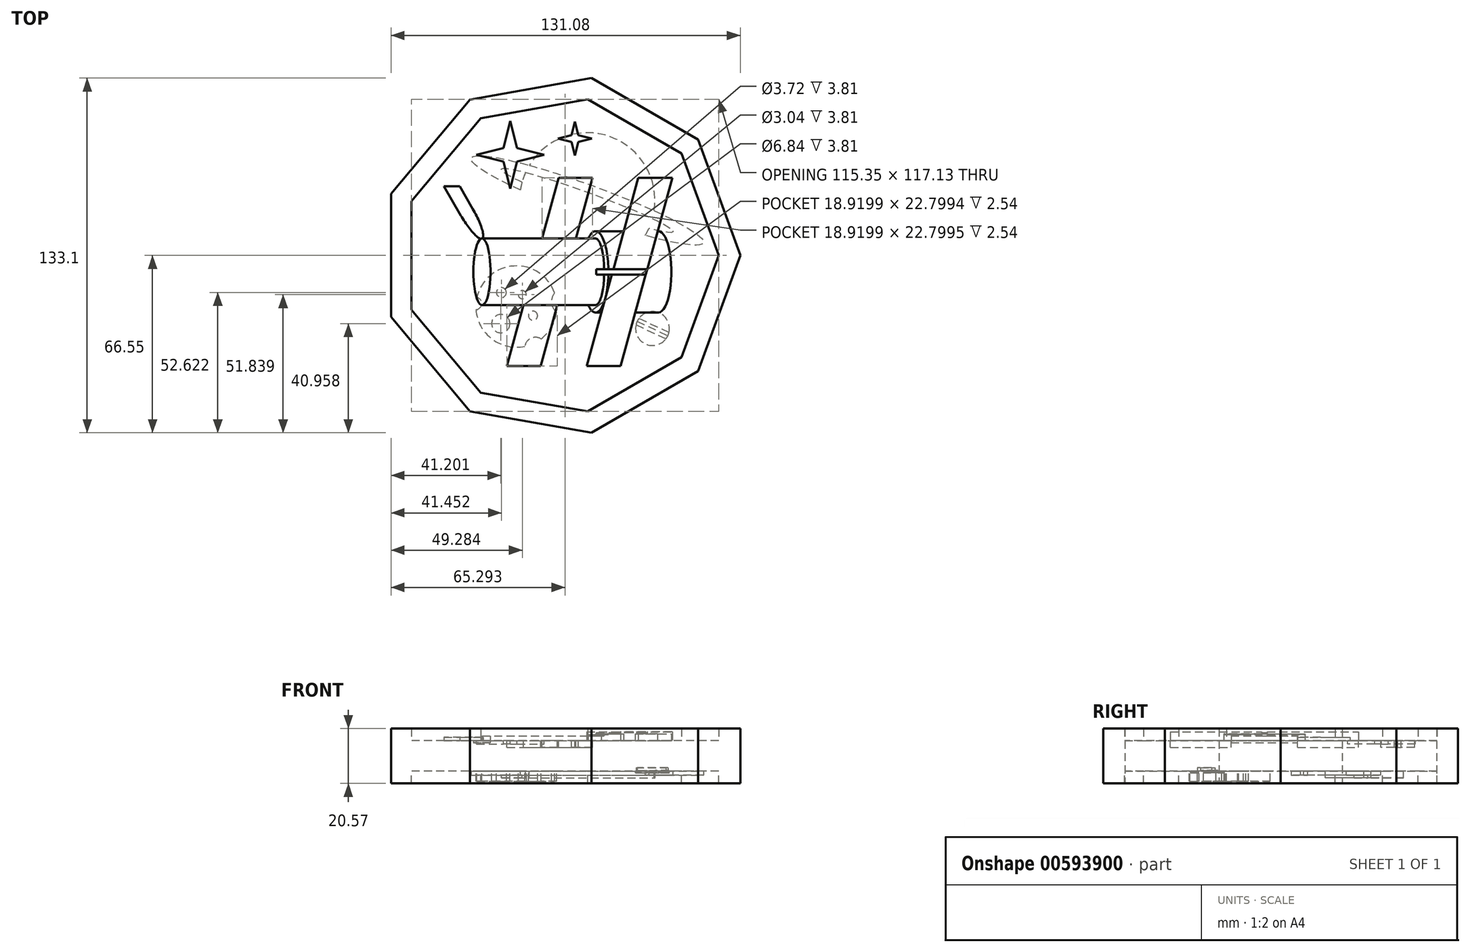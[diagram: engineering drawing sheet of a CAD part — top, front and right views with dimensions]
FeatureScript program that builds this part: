
annotation { "Feature Type Name" : "Feature", "Feature Type Description" : "" }
export const myFeature = defineFeature(function(context is Context, id is Id, definition is map)
    precondition{}
    {
        {
            var Q0;
            Q0=qCreatedBy(makeId("Top.planeOp"),FACE);
            var sketch = newSketch(context, id + "F0", { "sketchPlane" : qUnion([Q0])});
            skCircle(sketch, "E0.cCircle", {"center": v(0, 0) * mm, "radius": 63.5 * mm, "construction": true});
            skLineSegment(sketch, "E0.0", {"start": v(-63.5, -23.11) * mm, "end": v(-63.5, 23.11) * mm});
            skLineSegment(sketch, "E0.1", {"start": v(-63.5, 23.11) * mm, "end": v(-33.79, 58.52) * mm});
            skLineSegment(sketch, "E0.2", {"start": v(-33.79, 58.52) * mm, "end": v(11.73, 66.55) * mm});
            skLineSegment(sketch, "E0.3", {"start": v(11.73, 66.55) * mm, "end": v(51.77, 43.44) * mm});
            skLineSegment(sketch, "E0.4", {"start": v(51.77, 43.44) * mm, "end": v(67.58, 0) * mm});
            skLineSegment(sketch, "E0.5", {"start": v(67.58, 0) * mm, "end": v(51.77, -43.44) * mm});
            skLineSegment(sketch, "E0.6", {"start": v(51.77, -43.44) * mm, "end": v(11.73, -66.55) * mm});
            skLineSegment(sketch, "E0.7", {"start": v(11.73, -66.55) * mm, "end": v(-33.79, -58.52) * mm});
            skLineSegment(sketch, "E0.8", {"start": v(-33.79, -58.52) * mm, "end": v(-63.5, -23.11) * mm});
            skPoint(sketch, "E0.0.midPoint", {"position": v(-63.5, 0) * mm});
            skSolve(sketch);
        }
        {
            var Q0;
            Q0=makeQuery(id+"F0.imprint","IMPRINT",FACE,{"disambiguationData":[TD([[makeQuery(id+"F0.imprint","IMPRINT",EDGE,{"derivedFrom":sQuery(id+"F0.wireOp",EDGE,"E0.0")}),-1.0]])]});
            var sketch = newSketch(context, id + "F1", { "sketchPlane" : qUnion([Q0])});
            skCircle(sketch, "E1.cCircle", {"center": v(0, 0) * mm, "radius": 57.8 * mm, "construction": true});
            skLineSegment(sketch, "E1.0", {"start": v(-57.8, -21.04) * mm, "end": v(-57.8, 21.04) * mm});
            skLineSegment(sketch, "E1.1", {"start": v(-57.8, 21.04) * mm, "end": v(-30.76, 53.27) * mm});
            skLineSegment(sketch, "E1.2", {"start": v(-30.76, 53.27) * mm, "end": v(10.68, 60.58) * mm});
            skLineSegment(sketch, "E1.3", {"start": v(10.68, 60.58) * mm, "end": v(47.12, 39.54) * mm});
            skLineSegment(sketch, "E1.4", {"start": v(47.12, 39.54) * mm, "end": v(61.52, 0) * mm});
            skLineSegment(sketch, "E1.5", {"start": v(61.52, 0) * mm, "end": v(47.12, -39.54) * mm});
            skLineSegment(sketch, "E1.6", {"start": v(47.12, -39.54) * mm, "end": v(10.68, -60.58) * mm});
            skLineSegment(sketch, "E1.7", {"start": v(10.68, -60.58) * mm, "end": v(-30.76, -53.27) * mm});
            skLineSegment(sketch, "E1.8", {"start": v(-30.76, -53.27) * mm, "end": v(-57.8, -21.04) * mm});
            skPoint(sketch, "E1.0.midPoint", {"position": v(-57.8, 0) * mm});
            skSolve(sketch);
        }
        {
            var Q0;
            Q0=makeQuery(id+"F1.imprint","IMPRINT",FACE,{"disambiguationData":[TD([[makeQuery(id+"F1.imprint","IMPRINT",EDGE,{"derivedFrom":sQuery(id+"F1.wireOp",EDGE,"E1.0")}),1.0]])]});
            var Q1;
            Q1=makeQuery(id+"F1.imprint","IMPRINT",FACE,{"disambiguationData":[TD([[makeQuery(id+"F1.imprint","IMPRINT",EDGE,{"derivedFrom":sQuery(id+"F1.wireOp",EDGE,"E1.0")}),-1.0]])]});
            extrude(context, id + "F2", {"entities" : qUnion([Q0, Q1]), "depth" : 6.35 * mm, "offsetDistance" : 25.4 * mm});
        }
        {
            var Q0;
            Q0=makeQuery(id+"F2.opExtrude","CAP_FACE",FACE,{"disambiguationData":[OSD([sQuery(id+"F0.wireOp",EDGE,"E0.0"),sQuery(id+"F0.wireOp",EDGE,"E0.1"),sQuery(id+"F0.wireOp",EDGE,"E0.2"),sQuery(id+"F0.wireOp",EDGE,"E0.3"),sQuery(id+"F0.wireOp",EDGE,"E0.4"),sQuery(id+"F0.wireOp",EDGE,"E0.5"),sQuery(id+"F0.wireOp",EDGE,"E0.6"),sQuery(id+"F0.wireOp",EDGE,"E0.7"),sQuery(id+"F0.wireOp",EDGE,"E0.8")])],"isStart":false});
            var sketch = newSketch(context, id + "F3", { "sketchPlane" : qUnion([Q0])});
            skEllipse(sketch, "E2", {"center": v(-29.34, -6.15) * mm, "majorRadius": 12.5 * mm, "minorRadius": 3.22 * mm, "majorAxis": v(0, -1)});
            skEllipticalArc(sketch, "E3", {});
            skEllipticalArc(sketch, "E4", {});
            skEllipticalArc(sketch, "E5", {});
            skLineSegment(sketch, "E6", {"start": v(-29.28, 6.35) * mm, "end": v(13.3, 6.35) * mm});
            skLineSegment(sketch, "E7", {"start": v(-29.34, -18.64) * mm, "end": v(13.3, -18.64) * mm});
            skPoint(sketch, "E8.start.orphan", {"position": v(13.3, 9.1) * mm});
            skPoint(sketch, "E9.start.orphan", {"position": v(13.3, -21.39) * mm});
            skLineSegment(sketch, "E10", {"start": v(13.3, 9.1) * mm, "end": v(23.86, 9.1) * mm});
            skLineSegment(sketch, "E11", {"start": v(13.3, -21.39) * mm, "end": v(15.44, -21.39) * mm});
            skLineSegment(sketch, "E12.right", {"start": v(13.57, -7.15) * mm, "end": v(13.57, -5.14) * mm});
            skPoint(sketch, "E12.middle", {"position": v(16.77, -6.15) * mm});
            skLineSegment(sketch, "E13", {"start": v(19.98, -5.14) * mm, "end": v(29.34, 29.15) * mm});
            skLineSegment(sketch, "E14", {"start": v(29.34, 29.15) * mm, "end": v(42.04, 29.15) * mm});
            skLineSegment(sketch, "E15", {"start": v(42.04, 29.15) * mm, "end": v(32.68, -5.14) * mm});
            skLineSegment(sketch, "E16", {"start": v(9.97, -41.44) * mm, "end": v(19.32, -7.15) * mm});
            skLineSegment(sketch, "E17", {"start": v(9.97, -41.44) * mm, "end": v(22.67, -41.44) * mm});
            skLineSegment(sketch, "E18", {"start": v(32.02, -7.15) * mm, "end": v(22.67, -41.44) * mm});
            skLineSegment(sketch, "E19", {"start": v(-6.8, 6.35) * mm, "end": v(-0.58, 29.15) * mm});
            skLineSegment(sketch, "E20", {"start": v(-0.58, 29.15) * mm, "end": v(12.12, 29.15) * mm});
            skLineSegment(sketch, "E21", {"start": v(12.12, 29.15) * mm, "end": v(5.9, 6.35) * mm});
            skLineSegment(sketch, "E22", {"start": v(-19.94, -41.44) * mm, "end": v(-13.72, -18.64) * mm});
            skLineSegment(sketch, "E23", {"start": v(-19.94, -41.44) * mm, "end": v(-7.24, -41.44) * mm});
            skLineSegment(sketch, "E24", {"start": v(-1.02, -18.64) * mm, "end": v(-7.24, -41.44) * mm});
            skLineSegment(sketch, "E25.trimOffspring", {"start": v(28.14, -21.39) * mm, "end": v(36.92, -21.39) * mm});
            skEllipticalArc(sketch, "E26.trimOffspring", {});
            skEllipticalArc(sketch, "E27.trimOffspring", {});
            skLineSegment(sketch, "E28.trimOffspring", {"start": v(36.56, 9.1) * mm, "end": v(36.92, 9.1) * mm});
            skEllipticalArc(sketch, "E29", {});
            skLineSegment(sketch, "E30.left", {"start": v(-37.21, 14.96) * mm, "end": v(-43.56, 25.96) * mm});
            skLineSegment(sketch, "E31", {"start": v(-32.81, 17.5) * mm, "end": v(-37.7, 25.96) * mm});
            skLineSegment(sketch, "E32.0", {"start": v(-35.01, 16.23) * mm, "end": v(-32.81, 17.5) * mm, "construction": true});
            skLineSegment(sketch, "E32.1", {"start": v(-42.52, 28.12) * mm, "end": v(-42.52, 28.12) * mm});
            skLineSegment(sketch, "E33", {"start": v(-43.56, 25.96) * mm, "end": v(-37.7, 25.96) * mm});
            skEllipticalArc(sketch, "E34.trimOffspring", {});
            skEllipticalArc(sketch, "E35.trimOffspring", {});
            skPoint(sketch, "E36.orphan", {"position": v(-29.34, 6.35) * mm});
            skLineSegment(sketch, "E37", {"start": v(-29.34, 6.35) * mm, "end": v(-29.28, 6.35) * mm});
            skLineSegment(sketch, "E38", {"start": v(13.57, -5.14) * mm, "end": v(32.68, -5.14) * mm});
            skLineSegment(sketch, "E39", {"start": v(13.57, -7.15) * mm, "end": v(19.32, -7.15) * mm});
            skLineSegment(sketch, "E40", {"start": v(19.32, -7.15) * mm, "end": v(32.02, -7.15) * mm});
            skLineSegment(sketch, "E41", {"start": v(32.02, -7.15) * mm, "end": v(32.68, -5.14) * mm});
            const initialGuessF3  = {"E3": [0.013290015166545516, -0.006145414015407985, 0, -1, 0.012492057942954899, 0.00322138350000229, 0, 1.4905308017185153], "E4": [0.013290015166545516, -0.006145414015407985, 0, -1, 0.01524, 0.004816725737073453, 5.673256572594427, 0.7218980306940213], "E5": [0.036915319038134456, -0.006145414015407985, 0, -1, 0.01524, 0.004816725737073453, 0, 3.141592653589793], "E26.trimOffspring": [0.013290015166545516, -0.006145414015407985, 0, -1, 0.012492057942954899, 0.00322138350000229, 1.6510618518712803, 3.141592653589793], "E27.trimOffspring": [0.013290015166545516, -0.006145414015407985, 0, -1, 0.01524, 0.004816725737073453, 1.6365658647841919, 3.7515213881749525], "E29": [-0.03501228732094896, 0.01623190572703317, 0.5, -0.8660254037844387, 0.01143, 0.00254, 4.71238898038469, 6.123469424798111], "E34.trimOffspring": [-0.03501228732094896, 0.01623190572703317, 0.5, -0.8660254037844387, 0.01143, 0.00254, 0.010156128418935213, 1.5707963267948968], "E35.trimOffspring": [0.013290015166545516, -0.006145414015407985, 0, -1, 0.01524, 0.004816725737073453, 0.995530483120633, 1.5050267888056046]};
            skSetInitialGuess(sketch, initialGuessF3);
            skSolve(sketch);
        }
        {
            var Q0;
            {var subQ0=sQuery(id+"F3.wireOp",EDGE,"E19");Q0=makeQuery(id+"F3.imprint","IMPRINT",FACE,{"disambiguationData":[TD([[makeQuery(id+"F3.imprint","IMPRINT",EDGE,{"derivedFrom":subQ0}),-1.0]])]});}
            var Q1;
            {var subQ0=sQuery(id+"F3.wireOp",EDGE,"E22");Q1=makeQuery(id+"F3.imprint","IMPRINT",FACE,{"disambiguationData":[TD([[makeQuery(id+"F3.imprint","IMPRINT",EDGE,{"derivedFrom":subQ0}),-1.0]])]});}
            extrude(context, id + "F4", {"entities" : qUnion([Q0, Q1]), "operationType" : NewBodyOperationType.REMOVE, "oppositeDirection" : true, "depth" : 2.54 * mm, "offsetDistance" : 25.4 * mm});
        }
        {
            var Q0;
            {var subQ1=sQuery(id+"F3.wireOp",EDGE,"E3");Q0=makeQuery(id+"F3.imprint","IMPRINT",FACE,{"disambiguationData":[TD([[makeQuery(id+"F3.imprint","IMPRINT",EDGE,{"derivedFrom":subQ1}),1.0]])]});}
            extrude(context, id + "F5", {"entities" : qUnion([Q0]), "operationType" : NewBodyOperationType.ADD, "depth" : 1.78 * mm, "offsetDistance" : 25.4 * mm});
        }
        {
            var Q0;
            {var subQ6=sQuery(id+"F3.wireOp",EDGE,"E30.left");Q0=makeQuery(id+"F3.imprint","IMPRINT",FACE,{"disambiguationData":[TD([[makeQuery(id+"F3.imprint","IMPRINT",EDGE,{"derivedFrom":subQ6}),-1.0]])]});}
            extrude(context, id + "F6", {"entities" : qUnion([Q0]), "operationType" : NewBodyOperationType.ADD, "depth" : 1.27 * mm, "offsetDistance" : 25.4 * mm});
        }
        {
            var Q0;
            {var subQ1=sQuery(id+"F3.wireOp",EDGE,"E14");Q0=makeQuery(id+"F3.imprint","IMPRINT",FACE,{"disambiguationData":[TD([[makeQuery(id+"F3.imprint","IMPRINT",EDGE,{"derivedFrom":subQ1}),-1.0]])]});}
            var Q1;
            {var subQ5=sQuery(id+"F3.wireOp",EDGE,"E17");Q1=makeQuery(id+"F3.imprint","IMPRINT",FACE,{"disambiguationData":[TD([[makeQuery(id+"F3.imprint","IMPRINT",EDGE,{"derivedFrom":subQ5}),1.0]])]});}
            extrude(context, id + "F7", {"entities" : qUnion([Q0, Q1]), "operationType" : NewBodyOperationType.ADD, "depth" : 3.3 * mm, "offsetDistance" : 25.4 * mm});
        }
        {
            var Q0;
            {var subQ3=sQuery(id+"F3.wireOp",EDGE,"E12.right");Q0=makeQuery(id+"F3.imprint","IMPRINT",FACE,{"disambiguationData":[TD([[makeQuery(id+"F3.imprint","IMPRINT",EDGE,{"derivedFrom":subQ3}),-1.0]])]});}
            extrude(context, id + "F8", {"entities" : qUnion([Q0]), "operationType" : NewBodyOperationType.ADD, "depth" : 3.05 * mm, "offsetDistance" : 25.4 * mm});
        }
        {
            var Q0;
            {var subQ0=sQuery(id+"F3.wireOp",EDGE,"E2");var subQ1=makeQuery(id+"F3.imprint","INTERSECT",VERTEX,{"derivedFrom":[subQ0,sQuery(id+"F3.wireOp",EDGE,"E7")]});Q0=makeQuery(id+"F3.imprint","IMPRINT",FACE,{"disambiguationData":[TD([[makeQuery(id+"F3.imprint","IMPRINT",EDGE,{"disambiguationData":[TD([[subQ1,-1.0]])],"derivedFrom":subQ0}),1.0]])]});}
            extrude(context, id + "F9", {"entities" : qUnion([Q0]), "operationType" : NewBodyOperationType.REMOVE, "oppositeDirection" : true, "depth" : 0.76 * mm, "offsetDistance" : 25.4 * mm});
        }
        {
            var Q0;
            {var subQ0=sQuery(id+"F3.wireOp",EDGE,"E10");Q0=makeQuery(id+"F3.imprint","IMPRINT",FACE,{"disambiguationData":[TD([[makeQuery(id+"F3.imprint","IMPRINT",EDGE,{"derivedFrom":subQ0}),-1.0]])]});}
            var Q1;
            Q1=makeQuery(id+"F3.imprint","IMPRINT",FACE,{"disambiguationData":[TD([[makeQuery(id+"F3.imprint","IMPRINT",EDGE,{"derivedFrom":sQuery(id+"F3.wireOp",EDGE,"E5")}),1.0]])]});
            var Q2;
            {var subQ3=sQuery(id+"F3.wireOp",EDGE,"E35.trimOffspring");Q2=makeQuery(id+"F3.imprint","IMPRINT",FACE,{"disambiguationData":[TD([[makeQuery(id+"F3.imprint","IMPRINT",EDGE,{"derivedFrom":subQ3}),-1.0]])]});}
            var Q3;
            {var subQ0=sQuery(id+"F3.wireOp",EDGE,"E11");Q3=makeQuery(id+"F3.imprint","IMPRINT",FACE,{"disambiguationData":[TD([[makeQuery(id+"F3.imprint","IMPRINT",EDGE,{"derivedFrom":subQ0}),1.0]])]});}
            extrude(context, id + "F10", {"entities" : qUnion([Q0, Q1, Q2, Q3]), "operationType" : NewBodyOperationType.ADD, "depth" : 2.54 * mm, "offsetDistance" : 25.4 * mm});
        }
        {
            var Q0;
            {var subQ4=sQuery(id+"F3.wireOp",EDGE,"E3");Q0=makeQuery(id+"F3.imprint","IMPRINT",FACE,{"disambiguationData":[TD([[makeQuery(id+"F3.imprint","IMPRINT",EDGE,{"derivedFrom":subQ4}),-1.0]])]});}
            var Q1;
            {var subQ6=sQuery(id+"F3.wireOp",EDGE,"E26.trimOffspring");Q1=makeQuery(id+"F3.imprint","IMPRINT",FACE,{"disambiguationData":[TD([[makeQuery(id+"F3.imprint","IMPRINT",EDGE,{"derivedFrom":subQ6}),-1.0]])]});}
            extrude(context, id + "F11", {"entities" : qUnion([Q0, Q1]), "operationType" : NewBodyOperationType.ADD, "depth" : 2.3 * mm, "offsetDistance" : 25.4 * mm});
        }
        {
            var Q0;
            Q0=makeQuery(id+"F2.opExtrude","CAP_FACE",FACE,{"disambiguationData":[OSD([sQuery(id+"F0.wireOp",EDGE,"E0.0"),sQuery(id+"F0.wireOp",EDGE,"E0.1"),sQuery(id+"F0.wireOp",EDGE,"E0.2"),sQuery(id+"F0.wireOp",EDGE,"E0.3"),sQuery(id+"F0.wireOp",EDGE,"E0.4"),sQuery(id+"F0.wireOp",EDGE,"E0.5"),sQuery(id+"F0.wireOp",EDGE,"E0.6"),sQuery(id+"F0.wireOp",EDGE,"E0.7"),sQuery(id+"F0.wireOp",EDGE,"E0.8")])],"isStart":false});
            var sketch = newSketch(context, id + "F12", { "sketchPlane" : qUnion([Q0])});
            skPoint(sketch, "E42.middle", {"position": v(-32.68, 32.6) * mm});
            skLineSegment(sketch, "E43", {"start": v(-18.67, 50.43) * mm, "end": v(-21.21, 40.27) * mm});
            skLineSegment(sketch, "E44", {"start": v(-18.67, 50.43) * mm, "end": v(-16.13, 40.27) * mm});
            skLineSegment(sketch, "E45", {"start": v(-31.37, 37.73) * mm, "end": v(-21.21, 40.27) * mm});
            skLineSegment(sketch, "E46", {"start": v(-31.37, 37.73) * mm, "end": v(-21.21, 35.19) * mm});
            skLineSegment(sketch, "E47", {"start": v(-21.21, 35.19) * mm, "end": v(-18.67, 25.03) * mm});
            skLineSegment(sketch, "E48", {"start": v(-16.13, 35.19) * mm, "end": v(-18.67, 25.03) * mm});
            skLineSegment(sketch, "E49", {"start": v(-16.13, 40.27) * mm, "end": v(-5.97, 37.73) * mm});
            skLineSegment(sketch, "E50", {"start": v(-16.13, 35.19) * mm, "end": v(-5.97, 37.73) * mm});
            skPoint(sketch, "E51.middle", {"position": v(-8.99, 38.16) * mm});
            skLineSegment(sketch, "E52", {"start": v(0, 53.46) * mm, "end": v(-1.27, 48.38) * mm});
            skLineSegment(sketch, "E53", {"start": v(0, 53.46) * mm, "end": v(1.27, 48.38) * mm});
            skLineSegment(sketch, "E54", {"start": v(-6.35, 47.1) * mm, "end": v(-1.27, 48.38) * mm});
            skLineSegment(sketch, "E55", {"start": v(-6.35, 47.1) * mm, "end": v(-1.27, 45.84) * mm});
            skLineSegment(sketch, "E56", {"start": v(-1.27, 45.84) * mm, "end": v(0, 40.76) * mm});
            skLineSegment(sketch, "E57", {"start": v(1.27, 45.84) * mm, "end": v(0, 40.76) * mm});
            skLineSegment(sketch, "E58", {"start": v(1.27, 48.38) * mm, "end": v(6.35, 47.1) * mm});
            skLineSegment(sketch, "E59", {"start": v(1.27, 45.84) * mm, "end": v(6.35, 47.1) * mm});
            skPoint(sketch, "E60.start.orphan", {"position": v(-21.21, 37.73) * mm});
            skPoint(sketch, "E61.start.orphan", {"position": v(-18.67, 35.19) * mm});
            skPoint(sketch, "E62.start.orphan", {"position": v(-16.13, 37.73) * mm});
            skPoint(sketch, "E42.top.end.orphan", {"position": v(-18.67, 40.27) * mm});
            skPoint(sketch, "E63.start.orphan", {"position": v(-1.27, 47.1) * mm});
            skPoint(sketch, "E64.start.orphan", {"position": v(0, 48.38) * mm});
            skPoint(sketch, "E65.start.orphan", {"position": v(1.27, 47.1) * mm});
            skPoint(sketch, "E66.start.orphan", {"position": v(0, 45.84) * mm});
            skSolve(sketch);
        }
        {
            var Q0;
            Q0=makeQuery(id+"F12.imprint","IMPRINT",FACE,{"disambiguationData":[TD([[makeQuery(id+"F12.imprint","IMPRINT",EDGE,{"derivedFrom":sQuery(id+"F12.wireOp",EDGE,"E43")}),-1.0]])]});
            var sketch = newSketch(context, id + "F13", { "sketchPlane" : qUnion([Q0])});
            skCircle(sketch, "E67.cCircle", {"center": v(0, 0) * mm, "radius": 63.5 * mm, "construction": true});
            skLineSegment(sketch, "E67.0", {"start": v(-63.5, -23.11) * mm, "end": v(-63.5, 23.11) * mm});
            skLineSegment(sketch, "E67.1", {"start": v(-63.5, 23.11) * mm, "end": v(-33.79, 58.52) * mm});
            skLineSegment(sketch, "E67.2", {"start": v(-33.79, 58.52) * mm, "end": v(11.73, 66.55) * mm});
            skLineSegment(sketch, "E67.3", {"start": v(11.73, 66.55) * mm, "end": v(51.77, 43.44) * mm});
            skLineSegment(sketch, "E67.4", {"start": v(51.77, 43.44) * mm, "end": v(67.58, 0) * mm});
            skLineSegment(sketch, "E67.5", {"start": v(67.58, 0) * mm, "end": v(51.77, -43.44) * mm});
            skLineSegment(sketch, "E67.6", {"start": v(51.77, -43.44) * mm, "end": v(11.73, -66.55) * mm});
            skLineSegment(sketch, "E67.7", {"start": v(11.73, -66.55) * mm, "end": v(-33.79, -58.52) * mm});
            skLineSegment(sketch, "E67.8", {"start": v(-33.79, -58.52) * mm, "end": v(-63.5, -23.11) * mm});
            skPoint(sketch, "E67.0.midPoint", {"position": v(-63.5, 0) * mm});
            skCircle(sketch, "E68.cCircle", {"center": v(0, 0) * mm, "radius": 55.88 * mm, "construction": true});
            skLineSegment(sketch, "E68.0", {"start": v(-55.88, -20.34) * mm, "end": v(-55.88, 20.34) * mm});
            skLineSegment(sketch, "E68.1", {"start": v(-55.88, 20.34) * mm, "end": v(-29.73, 51.5) * mm});
            skLineSegment(sketch, "E68.2", {"start": v(-29.73, 51.5) * mm, "end": v(10.33, 58.56) * mm});
            skLineSegment(sketch, "E68.3", {"start": v(10.33, 58.56) * mm, "end": v(45.55, 38.22) * mm});
            skLineSegment(sketch, "E68.4", {"start": v(45.55, 38.22) * mm, "end": v(59.47, 0) * mm});
            skLineSegment(sketch, "E68.5", {"start": v(59.47, 0) * mm, "end": v(45.55, -38.22) * mm});
            skLineSegment(sketch, "E68.6", {"start": v(45.55, -38.22) * mm, "end": v(10.33, -58.56) * mm});
            skLineSegment(sketch, "E68.7", {"start": v(10.33, -58.56) * mm, "end": v(-29.73, -51.5) * mm});
            skLineSegment(sketch, "E68.8", {"start": v(-29.73, -51.5) * mm, "end": v(-55.88, -20.34) * mm});
            skPoint(sketch, "E68.0.midPoint", {"position": v(-55.88, 0) * mm});
            skSolve(sketch);
        }
        {
            var Q0;
            Q0=makeQuery(id+"F13.imprint","IMPRINT",FACE,{"disambiguationData":[TD([[makeQuery(id+"F13.imprint","IMPRINT",EDGE,{"derivedFrom":sQuery(id+"F13.wireOp",EDGE,"E67.0")}),-1.0]])]});
            extrude(context, id + "F14", {"entities" : qUnion([Q0]), "operationType" : NewBodyOperationType.ADD, "depth" : 4.57 * mm, "offsetDistance" : 25.4 * mm});
        }
        {
            var Q0;
            Q0=makeQuery(id+"F12.imprint","IMPRINT",FACE,{"disambiguationData":[TD([[makeQuery(id+"F12.imprint","IMPRINT",EDGE,{"derivedFrom":sQuery(id+"F12.wireOp",EDGE,"E43")}),1.0]])]});
            extrude(context, id + "F15", {"entities" : qUnion([Q0]), "operationType" : NewBodyOperationType.REMOVE, "oppositeDirection" : true, "depth" : 1.27 * mm, "offsetDistance" : 25.4 * mm});
        }
        {
            var Q0;
            Q0=makeQuery(id+"F3.imprint","IMPRINT",FACE,{"disambiguationData":[TD([[makeQuery(id+"F3.imprint","IMPRINT",EDGE,{"derivedFrom":sQuery(id+"F3.wireOp",EDGE,"E5")}),-1.0]])]});
            var sketch = newSketch(context, id + "F16", { "sketchPlane" : qUnion([Q0])});
            skLineSegment(sketch, "E69", {"start": v(5.52, 50.23) * mm, "end": v(4.25, 45.15) * mm});
            skLineSegment(sketch, "E70", {"start": v(5.52, 50.23) * mm, "end": v(6.79, 45.15) * mm});
            skLineSegment(sketch, "E71", {"start": v(-0.83, 43.88) * mm, "end": v(4.25, 45.15) * mm});
            skLineSegment(sketch, "E72", {"start": v(-0.83, 43.88) * mm, "end": v(4.25, 42.61) * mm});
            skLineSegment(sketch, "E73", {"start": v(4.25, 42.61) * mm, "end": v(5.52, 37.53) * mm});
            skLineSegment(sketch, "E74", {"start": v(6.79, 42.61) * mm, "end": v(5.52, 37.53) * mm});
            skLineSegment(sketch, "E75", {"start": v(6.79, 45.15) * mm, "end": v(11.87, 43.88) * mm});
            skLineSegment(sketch, "E76", {"start": v(6.79, 42.61) * mm, "end": v(11.87, 43.88) * mm});
            skPoint(sketch, "E77.start.orphan", {"position": v(4.25, 43.88) * mm});
            skPoint(sketch, "E78.start.orphan", {"position": v(5.52, 45.15) * mm});
            skPoint(sketch, "E79.start.orphan", {"position": v(6.79, 43.88) * mm});
            skPoint(sketch, "E80.start.orphan", {"position": v(5.52, 42.61) * mm});
            skSolve(sketch);
        }
        {
            var Q0;
            Q0=makeQuery(id+"F16.imprint","IMPRINT",FACE,{"disambiguationData":[TD([[makeQuery(id+"F16.imprint","IMPRINT",EDGE,{"derivedFrom":sQuery(id+"F16.wireOp",EDGE,"E69")}),1.0]])]});
            extrude(context, id + "F17", {"entities" : qUnion([Q0]), "operationType" : NewBodyOperationType.REMOVE, "oppositeDirection" : true, "depth" : 2.54 * mm, "offsetDistance" : 25.4 * mm});
        }
        {
            var Q0;
            Q0=makeQuery(id+"F0.imprint","IMPRINT",FACE,{"disambiguationData":[TD([[makeQuery(id+"F0.imprint","IMPRINT",EDGE,{"derivedFrom":sQuery(id+"F0.wireOp",EDGE,"E0.0")}),-1.0]])]});
            extrude(context, id + "F18", {"entities" : qUnion([Q0]), "operationType" : NewBodyOperationType.ADD, "oppositeDirection" : true, "depth" : 5.08 * mm, "offsetDistance" : 25.4 * mm});
        }
        {
            var Q0;
            Q0=makeQuery(id+"F18.opExtrude","CAP_FACE",FACE,{"disambiguationData":[OSD([sQuery(id+"F0.wireOp",EDGE,"E0.0"),sQuery(id+"F0.wireOp",EDGE,"E0.1"),sQuery(id+"F0.wireOp",EDGE,"E0.2"),sQuery(id+"F0.wireOp",EDGE,"E0.3"),sQuery(id+"F0.wireOp",EDGE,"E0.4"),sQuery(id+"F0.wireOp",EDGE,"E0.5"),sQuery(id+"F0.wireOp",EDGE,"E0.6"),sQuery(id+"F0.wireOp",EDGE,"E0.7"),sQuery(id+"F0.wireOp",EDGE,"E0.8")])],"isStart":false});
            var sketch = newSketch(context, id + "F19", { "sketchPlane" : qUnion([Q0])});
            skCircle(sketch, "E81.cCircle", {"center": v(0, 0) * mm, "radius": 55.88 * mm, "construction": true});
            skLineSegment(sketch, "E81.0", {"start": v(-55.88, -20.34) * mm, "end": v(-55.88, 20.34) * mm});
            skLineSegment(sketch, "E81.1", {"start": v(-55.88, 20.34) * mm, "end": v(-29.73, 51.5) * mm});
            skLineSegment(sketch, "E81.2", {"start": v(-29.73, 51.5) * mm, "end": v(10.33, 58.56) * mm});
            skLineSegment(sketch, "E81.3", {"start": v(10.33, 58.56) * mm, "end": v(45.55, 38.22) * mm});
            skLineSegment(sketch, "E81.4", {"start": v(45.55, 38.22) * mm, "end": v(59.47, 0) * mm});
            skLineSegment(sketch, "E81.5", {"start": v(59.47, 0) * mm, "end": v(45.55, -38.22) * mm});
            skLineSegment(sketch, "E81.6", {"start": v(45.55, -38.22) * mm, "end": v(10.33, -58.56) * mm});
            skLineSegment(sketch, "E81.7", {"start": v(10.33, -58.56) * mm, "end": v(-29.73, -51.5) * mm});
            skLineSegment(sketch, "E81.8", {"start": v(-29.73, -51.5) * mm, "end": v(-55.88, -20.34) * mm});
            skPoint(sketch, "E81.0.midPoint", {"position": v(-55.88, 0) * mm});
            skSolve(sketch);
        }
        {
            var Q0;
            Q0=makeQuery(id+"F19.imprint","IMPRINT",FACE,{"disambiguationData":[TD([[makeQuery(id+"F19.imprint","IMPRINT",EDGE,{"derivedFrom":sQuery(id+"F19.wireOp",EDGE,"E81.0")}),1.0]])]});
            extrude(context, id + "F20", {"entities" : qUnion([Q0]), "operationType" : NewBodyOperationType.ADD, "depth" : 4.57 * mm, "offsetDistance" : 25.4 * mm});
        }
        {
            var Q0;
            Q0=makeQuery(id+"F18.opExtrude","CAP_FACE",FACE,{"disambiguationData":[OSD([sQuery(id+"F0.wireOp",EDGE,"E0.0"),sQuery(id+"F0.wireOp",EDGE,"E0.1"),sQuery(id+"F0.wireOp",EDGE,"E0.2"),sQuery(id+"F0.wireOp",EDGE,"E0.3"),sQuery(id+"F0.wireOp",EDGE,"E0.4"),sQuery(id+"F0.wireOp",EDGE,"E0.5"),sQuery(id+"F0.wireOp",EDGE,"E0.6"),sQuery(id+"F0.wireOp",EDGE,"E0.7"),sQuery(id+"F0.wireOp",EDGE,"E0.8")])],"isStart":false});
            var sketch = newSketch(context, id + "F21", { "sketchPlane" : qUnion([Q0])});
            skArc(sketch, "E82", {"start": v(-11.57, -33.8) * mm, "mid": v(18.85, -44.52) * mm, "end": v(35.26, -16.76) * mm});
            skEllipticalArc(sketch, "E83", {});
            skEllipticalArc(sketch, "E84", {});
            skArc(sketch, "E85.trimOffspring", {"start": v(34.63, -13.84) * mm, "mid": v(1.47, 3.22) * mm, "end": v(-12.96, -31.16) * mm});
            const initialGuessF21  = {"E83": [0.010159997366546842, -0.020649188747997704, 0.9396926207859084, 0.3420201433256687, 0.046355, 0.005842, 2.1383146729930034, 1.0032779805967882], "E84": [0.010159997366546842, -0.020649188747997704, 0.9396926207859084, 0.3420201433256687, 0.03429, 0.002921, 2.4016551175536898, 0.7399375360360955]};
            skSetInitialGuess(sketch, initialGuessF21);
            skSolve(sketch);
        }
        {
            var Q0;
            {var subQ0=sQuery(id+"F21.wireOp",EDGE,"E85.trimOffspring");var subQ4=sQuery(id+"F21.wireOp",EDGE,"E84");var subQ6=makeQuery(id+"F21.imprint","INTERSECT",VERTEX,{"disambiguationData":[OD(2.0)],"derivedFrom":[subQ4,subQ0]});Q0=makeQuery(id+"F21.imprint","IMPRINT",FACE,{"disambiguationData":[TD([[makeQuery(id+"F21.imprint","IMPRINT",EDGE,{"disambiguationData":[TD([[subQ6,1.0]])],"derivedFrom":subQ4}),1.0]])]});}
            var Q1;
            {var subQ0=sQuery(id+"F21.wireOp",EDGE,"E82");Q1=makeQuery(id+"F21.imprint","IMPRINT",FACE,{"disambiguationData":[TD([[makeQuery(id+"F21.imprint","IMPRINT",EDGE,{"derivedFrom":subQ0}),1.0]])]});}
            extrude(context, id + "F22", {"entities" : qUnion([Q0, Q1]), "operationType" : NewBodyOperationType.ADD, "depth" : 2.54 * mm, "offsetDistance" : 25.4 * mm});
        }
        {
            var Q0;
            {var subQ4=sQuery(id+"F21.wireOp",EDGE,"E83");var subQ5=sQuery(id+"F21.wireOp",EDGE,"E82");var subQ8=makeQuery(id+"F21.imprint","INTERSECT",VERTEX,{"disambiguationData":[OD(0.0)],"derivedFrom":[subQ5,subQ4]});Q0=makeQuery(id+"F21.imprint","IMPRINT",FACE,{"disambiguationData":[TD([[makeQuery(id+"F21.imprint","IMPRINT",EDGE,{"disambiguationData":[TD([[subQ8,1.0]])],"derivedFrom":subQ4}),1.0]])]});}
            extrude(context, id + "F23", {"entities" : qUnion([Q0]), "operationType" : NewBodyOperationType.ADD, "depth" : 1.52 * mm, "offsetDistance" : 25.4 * mm});
        }
        {
            var Q0;
            Q0=makeQuery(id+"F23.boolean.opBoolean","SPLIT",FACE,{"disambiguationData":[TD([makeQuery(id+"F20.opExtrude","SWEPT_FACE",FACE,{"disambiguationData":[OSD([sQuery(id+"F19.wireOp",EDGE,"E81.0")])]}),makeQuery(id+"F20.opExtrude","SWEPT_FACE",FACE,{"disambiguationData":[OSD([sQuery(id+"F19.wireOp",EDGE,"E81.1")])]}),makeQuery(id+"F20.opExtrude","SWEPT_FACE",FACE,{"disambiguationData":[OSD([sQuery(id+"F19.wireOp",EDGE,"E81.2")])]}),makeQuery(id+"F20.opExtrude","SWEPT_FACE",FACE,{"disambiguationData":[OSD([sQuery(id+"F19.wireOp",EDGE,"E81.3")])]}),makeQuery(id+"F20.opExtrude","SWEPT_FACE",FACE,{"disambiguationData":[OSD([sQuery(id+"F19.wireOp",EDGE,"E81.4")])]}),makeQuery(id+"F20.opExtrude","SWEPT_FACE",FACE,{"disambiguationData":[OSD([sQuery(id+"F19.wireOp",EDGE,"E81.5")])]}),makeQuery(id+"F20.opExtrude","SWEPT_FACE",FACE,{"disambiguationData":[OSD([sQuery(id+"F19.wireOp",EDGE,"E81.6")])]}),makeQuery(id+"F20.opExtrude","SWEPT_FACE",FACE,{"disambiguationData":[OSD([sQuery(id+"F19.wireOp",EDGE,"E81.7")])]}),makeQuery(id+"F20.opExtrude","SWEPT_FACE",FACE,{"disambiguationData":[OSD([sQuery(id+"F19.wireOp",EDGE,"E81.8")])]}),makeQuery(id+"F22.opExtrude","SWEPT_FACE",FACE,{"disambiguationData":[OSD([sQuery(id+"F21.wireOp",EDGE,"E82")])]}),makeQuery(id+"F22.opExtrude","SWEPT_FACE",FACE,{"disambiguationData":[OSD([sQuery(id+"F21.wireOp",EDGE,"E85.trimOffspring")])]}),makeQuery(id+"F23.opExtrude","SWEPT_FACE",FACE,{"disambiguationData":[OSD([sQuery(id+"F21.wireOp",EDGE,"E83")])]})])],"derivedFrom":makeQuery(id+"F18.opExtrude","CAP_FACE",FACE,{"disambiguationData":[OSD([sQuery(id+"F0.wireOp",EDGE,"E0.0"),sQuery(id+"F0.wireOp",EDGE,"E0.1"),sQuery(id+"F0.wireOp",EDGE,"E0.2"),sQuery(id+"F0.wireOp",EDGE,"E0.3"),sQuery(id+"F0.wireOp",EDGE,"E0.4"),sQuery(id+"F0.wireOp",EDGE,"E0.5"),sQuery(id+"F0.wireOp",EDGE,"E0.6"),sQuery(id+"F0.wireOp",EDGE,"E0.7"),sQuery(id+"F0.wireOp",EDGE,"E0.8")])],"isStart":false})});
            var sketch = newSketch(context, id + "F24", { "sketchPlane" : qUnion([Q0])});
            skCircle(sketch, "E86", {"center": v(-16.42, 19.17) * mm, "radius": 15.24 * mm});
            skCircle(sketch, "E87", {"center": v(-22.3, 25.6) * mm, "radius": 3.42 * mm});
            skCircle(sketch, "E88", {"center": v(-10.19, 22.6) * mm, "radius": 1.7 * mm});
            skCircle(sketch, "E89", {"center": v(-22.05, 13.93) * mm, "radius": 1.86 * mm});
            skCircle(sketch, "E90", {"center": v(-14.22, 14.71) * mm, "radius": 1.52 * mm});
            skArc(sketch, "E91", {"start": v(-1.33, 21.3) * mm, "mid": v(-3.22, 17.82) * mm, "end": v(-2.07, 14.02) * mm});
            skArc(sketch, "E92", {"start": v(-31.27, 15.77) * mm, "mid": v(-29.44, 18.21) * mm, "end": v(-31.61, 20.36) * mm});
            skArc(sketch, "E93", {"start": v(-13.27, 34.08) * mm, "mid": v(-10.95, 31.08) * mm, "end": v(-7.17, 31.28) * mm});
            skCircle(sketch, "E94", {"center": v(34.65, 27.42) * mm, "radius": 6.35 * mm});
            skLineSegment(sketch, "E95", {"start": v(34.65, 27.42) * mm, "end": v(40.4, 30.1) * mm});
            skLineSegment(sketch, "E96", {"start": v(34.65, 27.42) * mm, "end": v(28.9, 24.74) * mm});
            skLineSegment(sketch, "E97", {"start": v(28.45, 26.02) * mm, "end": v(34.08, 28.64) * mm});
            skLineSegment(sketch, "E98", {"start": v(34.08, 28.64) * mm, "end": v(39.7, 31.27) * mm});
            skLineSegment(sketch, "E99", {"start": v(40.83, 28.9) * mm, "end": v(35.19, 26.26) * mm});
            skLineSegment(sketch, "E100", {"start": v(29.58, 23.6) * mm, "end": v(35.58, 26.45) * mm});
            skLineSegment(sketch, "E101.0", {"start": v(35.19, 26.26) * mm, "end": v(34.08, 28.64) * mm, "construction": true});
            skSolve(sketch);
        }
        {
            var Q0;
            {var subQ1=sQuery(id+"F24.wireOp",EDGE,"E95");Q0=makeQuery(id+"F24.imprint","IMPRINT",FACE,{"disambiguationData":[TD([[makeQuery(id+"F24.imprint","IMPRINT",EDGE,{"derivedFrom":subQ1}),1.0]])]});}
            extrude(context, id + "F25", {"entities" : qUnion([Q0]), "operationType" : NewBodyOperationType.REMOVE, "oppositeDirection" : true, "depth" : 1.27 * mm, "offsetDistance" : 25.4 * mm});
        }
        {
            var Q0;
            {var subQ0=sQuery(id+"F24.wireOp",EDGE,"E95");Q0=makeQuery(id+"F24.imprint","IMPRINT",FACE,{"disambiguationData":[TD([[makeQuery(id+"F24.imprint","IMPRINT",EDGE,{"derivedFrom":subQ0}),-1.0]])]});}
            extrude(context, id + "F26", {"entities" : qUnion([Q0]), "operationType" : NewBodyOperationType.REMOVE, "oppositeDirection" : true, "depth" : 0.36 * mm, "offsetDistance" : 25.4 * mm});
        }
        {
            var Q0;
            {var subQ0=sQuery(id+"F24.wireOp",EDGE,"E97");Q0=makeQuery(id+"F24.imprint","IMPRINT",FACE,{"disambiguationData":[TD([[makeQuery(id+"F24.imprint","IMPRINT",EDGE,{"derivedFrom":subQ0}),1.0]])]});}
            var Q1;
            {var subQ3=sQuery(id+"F24.wireOp",EDGE,"E100");Q1=makeQuery(id+"F24.imprint","IMPRINT",FACE,{"disambiguationData":[TD([[makeQuery(id+"F24.imprint","IMPRINT",EDGE,{"derivedFrom":subQ3}),-1.0]])]});}
            extrude(context, id + "F27", {"entities" : qUnion([Q0, Q1]), "operationType" : NewBodyOperationType.ADD, "depth" : 0.64 * mm, "offsetDistance" : 25.4 * mm});
        }
        {
            var Q0;
            Q0=makeQuery(id+"F24.imprint","IMPRINT",FACE,{"disambiguationData":[TD([[makeQuery(id+"F24.imprint","IMPRINT",EDGE,{"derivedFrom":sQuery(id+"F24.wireOp",EDGE,"E87")}),-1.0]])]});
            extrude(context, id + "F28", {"entities" : qUnion([Q0]), "operationType" : NewBodyOperationType.ADD, "depth" : 3.8 * mm, "offsetDistance" : 25.4 * mm});
        }
    });
